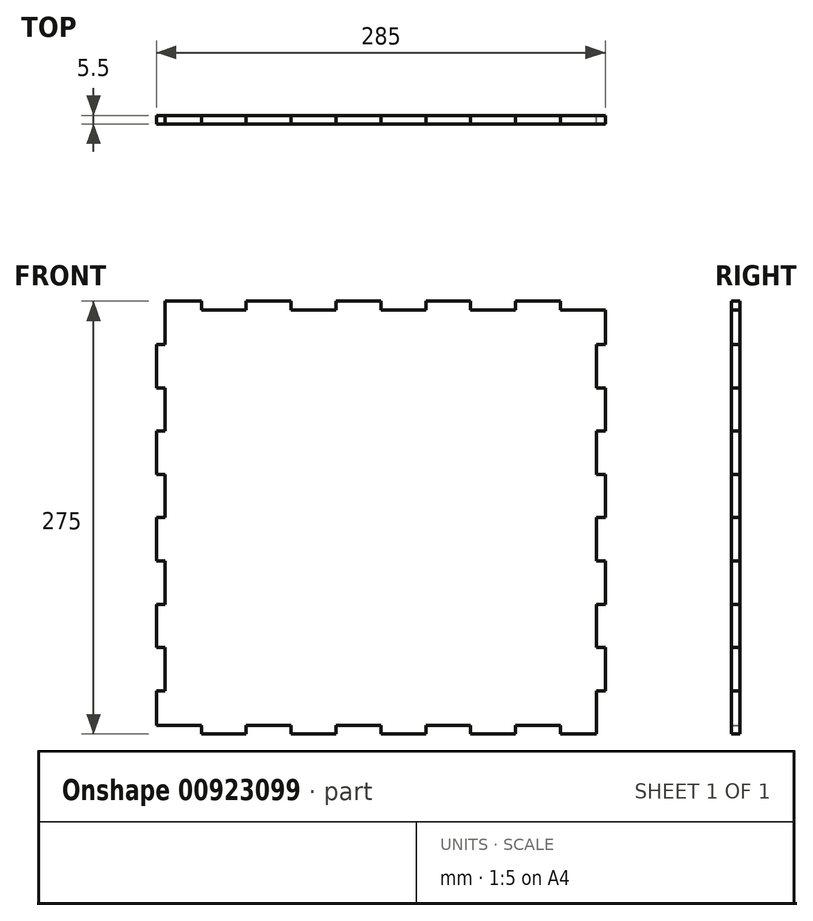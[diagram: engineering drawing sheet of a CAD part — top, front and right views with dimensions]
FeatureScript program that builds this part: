
annotation { "Feature Type Name" : "Feature", "Feature Type Description" : "" }
export const myFeature = defineFeature(function(context is Context, id is Id, definition is map)
    precondition{}
    {
        {
            var Q0;
            Q0=qCreatedBy(makeId("Front.planeOp"),FACE);
            var sketch = newSketch(context, id + "F0", { "sketchPlane" : qUnion([Q0])});
            skLineSegment(sketch, "E0.bottom", {"start": v(142.5, -137.5) * mm, "end": v(-142.5, -137.5) * mm, "construction": true});
            skLineSegment(sketch, "E0.top", {"start": v(142.5, 137.5) * mm, "end": v(-142.5, 137.5) * mm, "construction": true});
            skLineSegment(sketch, "E0.left", {"start": v(142.5, -137.5) * mm, "end": v(142.5, 137.5) * mm, "construction": true});
            skLineSegment(sketch, "E0.right", {"start": v(-142.5, -137.5) * mm, "end": v(-142.5, 137.5) * mm, "construction": true});
            skPoint(sketch, "E0.middle", {"position": v(0, 0) * mm});
            skLineSegment(sketch, "E1", {"start": v(-137, 137.5) * mm, "end": v(-137, 110) * mm});
            skLineSegment(sketch, "E2", {"start": v(-137, 110) * mm, "end": v(-142.5, 110) * mm});
            skLineSegment(sketch, "E3", {"start": v(-142.5, 110) * mm, "end": v(-142.5, 82.5) * mm});
            skLineSegment(sketch, "E4", {"start": v(-142.5, 82.5) * mm, "end": v(-137, 82.5) * mm});
            skLineSegment(sketch, "E5", {"start": v(-137, 82.5) * mm, "end": v(-137, 55) * mm});
            skLineSegment(sketch, "E6", {"start": v(-137, 55) * mm, "end": v(-142.5, 55) * mm});
            skLineSegment(sketch, "E7", {"start": v(-142.5, 55) * mm, "end": v(-142.5, 27.5) * mm});
            skLineSegment(sketch, "E8", {"start": v(-142.5, 27.5) * mm, "end": v(-137, 27.5) * mm});
            skLineSegment(sketch, "E9", {"start": v(-137, 27.5) * mm, "end": v(-137, 0) * mm});
            skLineSegment(sketch, "E10", {"start": v(-137, 0) * mm, "end": v(-142.5, 0) * mm});
            skLineSegment(sketch, "E11", {"start": v(-142.5, 0) * mm, "end": v(-142.5, -27.5) * mm});
            skLineSegment(sketch, "E12", {"start": v(-142.5, -27.5) * mm, "end": v(-137, -27.5) * mm});
            skLineSegment(sketch, "E13", {"start": v(-137, -27.5) * mm, "end": v(-137, -55) * mm});
            skLineSegment(sketch, "E14", {"start": v(-137, -55) * mm, "end": v(-142.5, -55) * mm});
            skLineSegment(sketch, "E15", {"start": v(-142.5, -55) * mm, "end": v(-142.5, -82.5) * mm});
            skLineSegment(sketch, "E16", {"start": v(-142.5, -82.5) * mm, "end": v(-137, -82.5) * mm});
            skLineSegment(sketch, "E17", {"start": v(-137, -82.5) * mm, "end": v(-137, -110) * mm});
            skLineSegment(sketch, "E18", {"start": v(-137, -110) * mm, "end": v(-142.5, -110) * mm});
            skLineSegment(sketch, "E19", {"start": v(-142.5, -110) * mm, "end": v(-142.5, -137.5) * mm});
            skLineSegment(sketch, "E20", {"start": v(-40, 100) * mm, "end": v(40, 100) * mm, "construction": true});
            skLineSegment(sketch, "E21", {"start": v(0, 100) * mm, "end": v(0, 0) * mm, "construction": true});
            skArc(sketch, "E22.0.startCap", {"start": v(-40, 87.5) * mm, "mid": v(-52.5, 100) * mm, "end": v(-40, 112.5) * mm, "construction": true});
            skArc(sketch, "E22.0.endCap", {"start": v(40, 112.5) * mm, "mid": v(52.5, 100) * mm, "end": v(40, 87.5) * mm, "construction": true});
            skLineSegment(sketch, "E22.0.left", {"start": v(-40, 112.5) * mm, "end": v(40, 112.5) * mm, "construction": true});
            skLineSegment(sketch, "E22.0.right", {"start": v(-40, 87.5) * mm, "end": v(40, 87.5) * mm, "construction": true});
            skLineSegment(sketch, "E23", {"start": v(-142.5, -132) * mm, "end": v(-114, -132) * mm});
            skLineSegment(sketch, "E24", {"start": v(-114, -132) * mm, "end": v(-114, -137.5) * mm});
            skLineSegment(sketch, "E25", {"start": v(-114, -137.5) * mm, "end": v(-85.5, -137.5) * mm});
            skLineSegment(sketch, "E26", {"start": v(-85.5, -137.5) * mm, "end": v(-85.5, -132) * mm});
            skLineSegment(sketch, "E27", {"start": v(-85.5, -132) * mm, "end": v(-57, -132) * mm});
            skLineSegment(sketch, "E28", {"start": v(-57, -132) * mm, "end": v(-57, -137.5) * mm});
            skLineSegment(sketch, "E29", {"start": v(-57, -137.5) * mm, "end": v(-28.5, -137.5) * mm});
            skLineSegment(sketch, "E30", {"start": v(-28.5, -137.5) * mm, "end": v(-28.5, -132) * mm});
            skLineSegment(sketch, "E31", {"start": v(-28.5, -132) * mm, "end": v(0, -132) * mm});
            skLineSegment(sketch, "E32", {"start": v(0, -132) * mm, "end": v(0, -137.5) * mm});
            skLineSegment(sketch, "E33", {"start": v(0, -137.5) * mm, "end": v(28.5, -137.5) * mm});
            skLineSegment(sketch, "E34", {"start": v(28.5, -137.5) * mm, "end": v(28.5, -132) * mm});
            skLineSegment(sketch, "E35", {"start": v(28.5, -132) * mm, "end": v(57, -132) * mm});
            skLineSegment(sketch, "E36", {"start": v(57, -132) * mm, "end": v(57, -137.5) * mm});
            skLineSegment(sketch, "E37", {"start": v(57, -137.5) * mm, "end": v(85.5, -137.5) * mm});
            skLineSegment(sketch, "E38", {"start": v(85.5, -137.5) * mm, "end": v(85.5, -132) * mm});
            skLineSegment(sketch, "E39", {"start": v(85.5, -132) * mm, "end": v(114, -132) * mm});
            skLineSegment(sketch, "E40", {"start": v(114, -132) * mm, "end": v(114, -137.5) * mm});
            skLineSegment(sketch, "E41", {"start": v(114, -137.5) * mm, "end": v(142.5, -137.5) * mm});
            skLineSegment(sketch, "E42", {"start": v(137, -137.5) * mm, "end": v(137, -110) * mm});
            skLineSegment(sketch, "E43", {"start": v(137, -110) * mm, "end": v(142.5, -110) * mm});
            skLineSegment(sketch, "E44", {"start": v(142.5, -110) * mm, "end": v(142.5, -82.5) * mm});
            skLineSegment(sketch, "E45", {"start": v(142.5, -82.5) * mm, "end": v(137, -82.5) * mm});
            skLineSegment(sketch, "E46", {"start": v(137, -82.5) * mm, "end": v(137, -55) * mm});
            skLineSegment(sketch, "E47", {"start": v(137, -55) * mm, "end": v(142.5, -55) * mm});
            skLineSegment(sketch, "E48", {"start": v(142.5, -55) * mm, "end": v(142.5, -27.5) * mm});
            skLineSegment(sketch, "E49", {"start": v(142.5, -27.5) * mm, "end": v(137, -27.5) * mm});
            skLineSegment(sketch, "E50", {"start": v(137, -27.5) * mm, "end": v(137, 0) * mm});
            skLineSegment(sketch, "E51", {"start": v(137, 0) * mm, "end": v(142.5, 0) * mm});
            skLineSegment(sketch, "E52", {"start": v(142.5, 0) * mm, "end": v(142.5, 27.5) * mm});
            skLineSegment(sketch, "E53", {"start": v(142.5, 27.5) * mm, "end": v(137, 27.5) * mm});
            skLineSegment(sketch, "E54", {"start": v(137, 27.5) * mm, "end": v(137, 55) * mm});
            skLineSegment(sketch, "E55", {"start": v(137, 55) * mm, "end": v(142.5, 55) * mm});
            skLineSegment(sketch, "E56", {"start": v(142.5, 55) * mm, "end": v(142.5, 82.5) * mm});
            skLineSegment(sketch, "E57", {"start": v(142.5, 82.5) * mm, "end": v(137, 82.5) * mm});
            skLineSegment(sketch, "E58", {"start": v(137, 82.5) * mm, "end": v(137, 110) * mm});
            skLineSegment(sketch, "E59", {"start": v(137, 110) * mm, "end": v(142.5, 110) * mm});
            skLineSegment(sketch, "E60", {"start": v(142.5, 110) * mm, "end": v(142.5, 137.5) * mm});
            skLineSegment(sketch, "E61", {"start": v(142.5, 132) * mm, "end": v(114, 132) * mm});
            skLineSegment(sketch, "E62", {"start": v(114, 132) * mm, "end": v(114, 137.5) * mm});
            skLineSegment(sketch, "E63", {"start": v(114, 137.5) * mm, "end": v(85.5, 137.5) * mm});
            skLineSegment(sketch, "E64", {"start": v(85.5, 137.5) * mm, "end": v(85.5, 132) * mm});
            skLineSegment(sketch, "E65", {"start": v(85.5, 132) * mm, "end": v(57, 132) * mm});
            skLineSegment(sketch, "E66", {"start": v(57, 132) * mm, "end": v(57, 137.5) * mm});
            skLineSegment(sketch, "E67", {"start": v(57, 137.5) * mm, "end": v(28.5, 137.5) * mm});
            skLineSegment(sketch, "E68", {"start": v(28.5, 137.5) * mm, "end": v(28.5, 132) * mm});
            skLineSegment(sketch, "E69", {"start": v(28.5, 132) * mm, "end": v(0, 132) * mm});
            skLineSegment(sketch, "E70", {"start": v(0, 132) * mm, "end": v(0, 137.5) * mm});
            skLineSegment(sketch, "E71", {"start": v(0, 137.5) * mm, "end": v(-28.5, 137.5) * mm});
            skLineSegment(sketch, "E72", {"start": v(-28.5, 137.5) * mm, "end": v(-28.5, 132) * mm});
            skLineSegment(sketch, "E73", {"start": v(-28.5, 132) * mm, "end": v(-57, 132) * mm});
            skLineSegment(sketch, "E74", {"start": v(-57, 132) * mm, "end": v(-57, 137.5) * mm});
            skLineSegment(sketch, "E75", {"start": v(-57, 137.5) * mm, "end": v(-85.5, 137.5) * mm});
            skLineSegment(sketch, "E76", {"start": v(-85.5, 137.5) * mm, "end": v(-85.5, 132) * mm});
            skLineSegment(sketch, "E77", {"start": v(-85.5, 132) * mm, "end": v(-114, 132) * mm});
            skLineSegment(sketch, "E78", {"start": v(-114, 132) * mm, "end": v(-114, 137.5) * mm});
            skLineSegment(sketch, "E79", {"start": v(-114, 137.5) * mm, "end": v(-142.5, 137.5) * mm});
            skSolve(sketch);
        }
        {
            var Q0;
            Q0=qSketchRegion(id+"F0",true);
            extrude(context, id + "F1", {"entities" : qUnion([Q0]), "depth" : 5.5 * mm, "offsetDistance" : 25 * mm});
        }
    });
